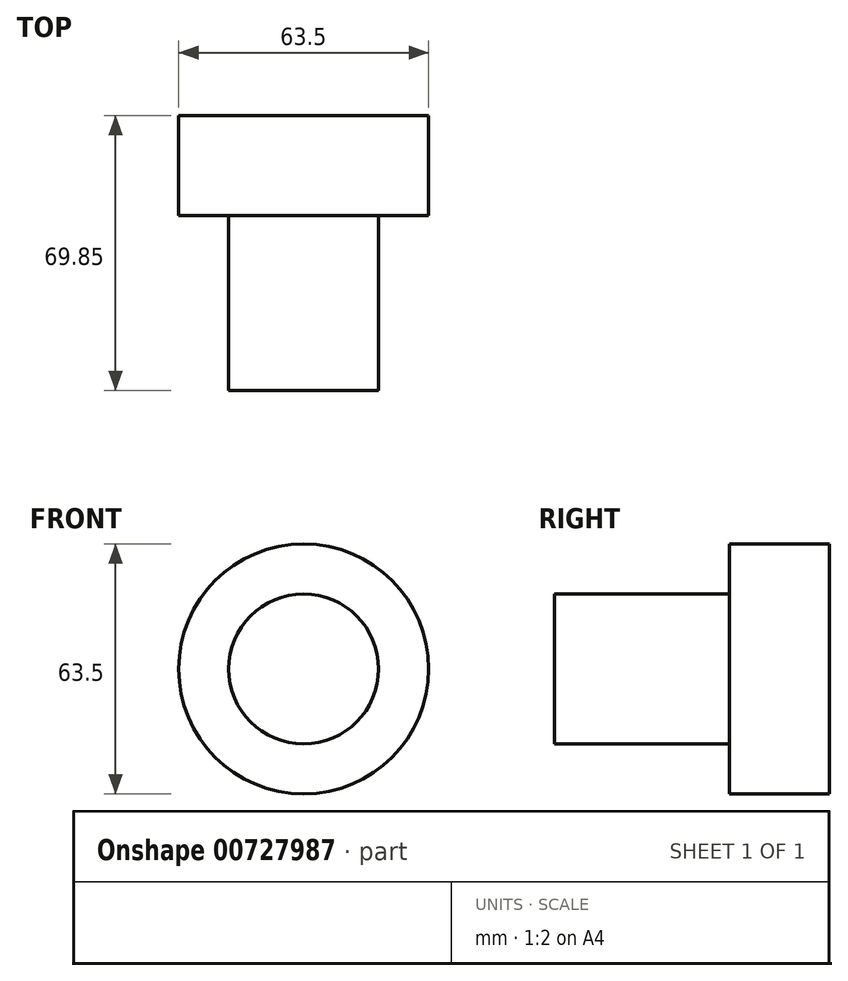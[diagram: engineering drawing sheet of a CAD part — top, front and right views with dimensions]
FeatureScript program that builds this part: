
annotation { "Feature Type Name" : "Feature", "Feature Type Description" : "" }
export const myFeature = defineFeature(function(context is Context, id is Id, definition is map)
    precondition{}
    {
        {
            var Q0;
            Q0=qCreatedBy(makeId("Front.planeOp"),FACE);
            var sketch = newSketch(context, id + "F0", { "sketchPlane" : qUnion([Q0])});
            skCircle(sketch, "E0", {"center": v(0, 0) * mm, "radius": 31.75 * mm});
            skCircle(sketch, "E1", {"center": v(0, 0) * mm, "radius": 19.05 * mm});
            skSolve(sketch);
        }
        {
            var Q0;
            Q0=makeQuery(id+"F0.imprint","IMPRINT",FACE,{"disambiguationData":[TD([[makeQuery(id+"F0.imprint","IMPRINT",EDGE,{"derivedFrom":sQuery(id+"F0.wireOp",EDGE,"E1")}),1.0]])]});
            extrude(context, id + "F1", {"entities" : qUnion([Q0]), "depth" : 44.45 * mm, "offsetDistance" : 25.4 * mm});
        }
        {
            var Q0;
            Q0 = qSketchRegion(id + "F0", true);
            extrude(context, id + "F2", {"entities" : qUnion([Q0]), "operationType" : NewBodyOperationType.ADD, "depth" : 25.4 * mm, "offsetDistance" : 25.4 * mm});
        }
        {
            var Q0;
            Q0=makeQuery(id+"F1.opExtrude","CAP_FACE",FACE,{"disambiguationData":[OSD([sQuery(id+"F0.wireOp",EDGE,"E1")])],"isStart":false});
            extrude(context, id + "F3", {"entities" : qUnion([Q0]), "operationType" : NewBodyOperationType.ADD, "depth" : 25.4 * mm, "offsetDistance" : 25.4 * mm});
        }
    });
